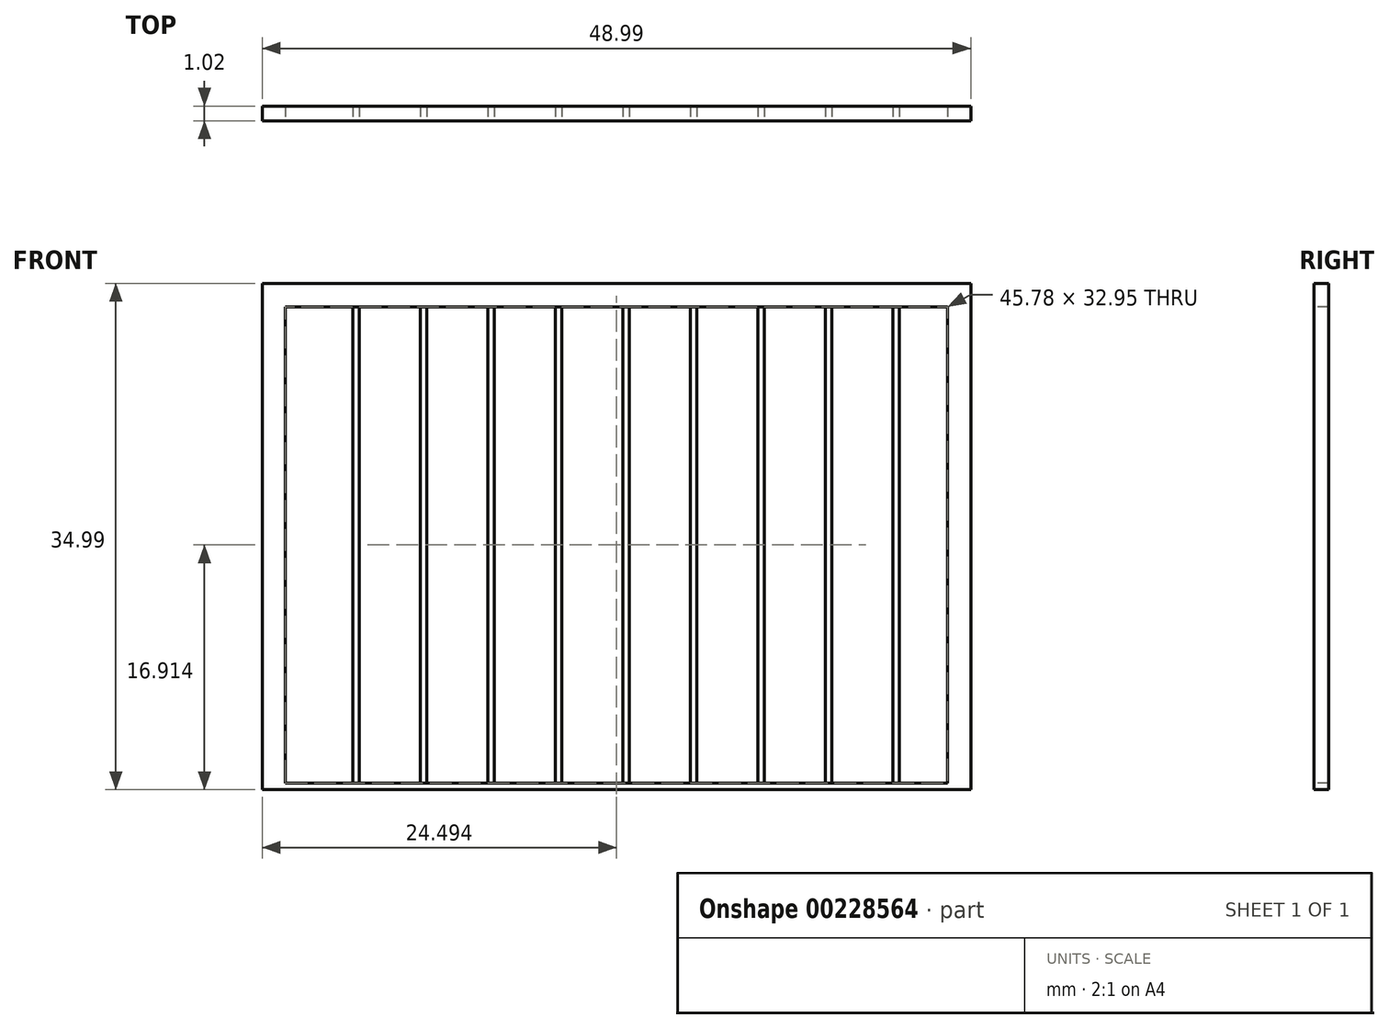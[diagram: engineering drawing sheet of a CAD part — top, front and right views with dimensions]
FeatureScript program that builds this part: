
annotation { "Feature Type Name" : "Feature", "Feature Type Description" : "" }
export const myFeature = defineFeature(function(context is Context, id is Id, definition is map)
    precondition{}
    {
        {
            var Q0;
            Q0=qCreatedBy(makeId("Front.planeOp"),FACE);
            var sketch = newSketch(context, id + "F0", { "sketchPlane" : qUnion([Q0])});
            skLineSegment(sketch, "E0.bottom", {"start": v(0, 0) * mm, "end": v(-4267.2, 0) * mm});
            skLineSegment(sketch, "E0.top", {"start": v(0, 3048) * mm, "end": v(-4267.2, 3048) * mm});
            skLineSegment(sketch, "E0.left", {"start": v(0, 0) * mm, "end": v(0, 3048) * mm});
            skLineSegment(sketch, "E0.right", {"start": v(-4267.2, 0) * mm, "end": v(-4267.2, 3048) * mm});
            skSolve(sketch);
        }
        {
            var Q0;
            Q0=makeQuery(id+"F0.imprint","IMPRINT",FACE,{"disambiguationData":[TD([[makeQuery(id+"F0.imprint","IMPRINT",EDGE,{"derivedFrom":sQuery(id+"F0.wireOp",EDGE,"E0.bottom")}),-1.0]])]});
            extrude(context, id + "F1", {"entities" : qUnion([Q0]), "depth" : 88.9 * mm});
        }
        {
            var Q0;
            Q0=makeQuery(id+"F1.opExtrude","CAP_FACE",FACE,{"disambiguationData":[OSD([sQuery(id+"F0.wireOp",EDGE,"E0.bottom"),sQuery(id+"F0.wireOp",EDGE,"E0.top"),sQuery(id+"F0.wireOp",EDGE,"E0.left"),sQuery(id+"F0.wireOp",EDGE,"E0.right")])],"isStart":true});
            var sketch = newSketch(context, id + "F2", { "sketchPlane" : qUnion([Q0])});
            skLineSegment(sketch, "E1", {"start": v(139.7, 0) * mm, "end": v(139.7, 2908.3) * mm});
            skLineSegment(sketch, "E2", {"start": v(139.7, 2908.3) * mm, "end": v(4127.5, 2908.3) * mm});
            skLineSegment(sketch, "E3", {"start": v(4127.5, 2908.3) * mm, "end": v(4127.5, 0) * mm});
            skLineSegment(sketch, "E4", {"start": v(4127.5, 0) * mm, "end": v(139.7, 0) * mm});
            skSolve(sketch);
        }
        {
            var Q0;
            Q0=makeQuery(id+"F2.imprint","IMPRINT",FACE,{"disambiguationData":[TD([[makeQuery(id+"F2.imprint","IMPRINT",EDGE,{"derivedFrom":sQuery(id+"F2.wireOp",EDGE,"E1")}),-1.0]])]});
            extrude(context, id + "F3", {"entities" : qUnion([Q0]), "operationType" : NewBodyOperationType.REMOVE, "endBound" : BoundingType.THROUGH_ALL, "oppositeDirection" : true, "depth" : 25.4 * mm});
        }
        {
            var Q0;
            Q0=makeQuery(id+"F1.opExtrude","CAP_FACE",FACE,{"disambiguationData":[OSD([sQuery(id+"F0.wireOp",EDGE,"E0.bottom"),sQuery(id+"F0.wireOp",EDGE,"E0.top"),sQuery(id+"F0.wireOp",EDGE,"E0.left"),sQuery(id+"F0.wireOp",EDGE,"E0.right")])],"isStart":false});
            var sketch = newSketch(context, id + "F4", { "sketchPlane" : qUnion([Q0])});
            skLineSegment(sketch, "E5.bottom", {"start": v(-4127.5, 0) * mm, "end": v(-139.7, 0) * mm});
            skLineSegment(sketch, "E5.top", {"start": v(-4127.5, 38.1) * mm, "end": v(-139.7, 38.1) * mm});
            skLineSegment(sketch, "E5.left", {"start": v(-4127.5, 0) * mm, "end": v(-4127.5, 38.1) * mm});
            skLineSegment(sketch, "E5.right", {"start": v(-139.7, 0) * mm, "end": v(-139.7, 38.1) * mm});
            skSolve(sketch);
        }
        {
            var Q0;
            Q0=makeQuery(id+"F4.imprint","IMPRINT",FACE,{"disambiguationData":[TD([[makeQuery(id+"F4.imprint","IMPRINT",EDGE,{"derivedFrom":sQuery(id+"F4.wireOp",EDGE,"E5.bottom")}),1.0]])]});
            extrude(context, id + "F5", {"entities" : qUnion([Q0]), "operationType" : NewBodyOperationType.ADD, "oppositeDirection" : true, "depth" : 88.9 * mm});
        }
        {
            var Q0;
            Q0=makeQuery(id+"F5.boolean.opBoolean","MERGE",FACE,{"derivedFrom":[makeQuery(id+"F1.opExtrude","CAP_FACE",FACE,{"disambiguationData":[OSD([sQuery(id+"F0.wireOp",EDGE,"E0.bottom"),sQuery(id+"F0.wireOp",EDGE,"E0.top"),sQuery(id+"F0.wireOp",EDGE,"E0.left"),sQuery(id+"F0.wireOp",EDGE,"E0.right")])],"isStart":false}),makeQuery(id+"F5.opExtrude","CAP_FACE",FACE,{"disambiguationData":[OSD([sQuery(id+"F4.wireOp",EDGE,"E5.bottom"),sQuery(id+"F4.wireOp",EDGE,"E5.top"),sQuery(id+"F4.wireOp",EDGE,"E5.left"),sQuery(id+"F4.wireOp",EDGE,"E5.right")])],"isStart":true})]});
            var sketch = newSketch(context, id + "F6", { "sketchPlane" : qUnion([Q0])});
            skLineSegment(sketch, "E6.bottom", {"start": v(-3721.1, 38.1) * mm, "end": v(-3683, 38.1) * mm});
            skLineSegment(sketch, "E6.top", {"start": v(-3721.1, 2908.3) * mm, "end": v(-3683, 2908.3) * mm});
            skLineSegment(sketch, "E6.left", {"start": v(-3721.1, 38.1) * mm, "end": v(-3721.1, 2908.3) * mm});
            skLineSegment(sketch, "E6.right", {"start": v(-3683, 38.1) * mm, "end": v(-3683, 2908.3) * mm});
            skLineSegment(sketch, "E7.1.0.0", {"start": v(-3314.7, 38.1) * mm, "end": v(-3314.7, 2908.3) * mm});
            skLineSegment(sketch, "E7.1.0.1", {"start": v(-3276.6, 38.1) * mm, "end": v(-3276.6, 2908.3) * mm});
            skLineSegment(sketch, "E7.1.0.2", {"start": v(-3314.7, 38.1) * mm, "end": v(-3276.6, 38.1) * mm});
            skLineSegment(sketch, "E7.1.0.3", {"start": v(-3314.7, 2908.3) * mm, "end": v(-3276.6, 2908.3) * mm});
            skLineSegment(sketch, "E7.2.0.0", {"start": v(-2908.3, 38.1) * mm, "end": v(-2908.3, 2908.3) * mm});
            skLineSegment(sketch, "E7.2.0.1", {"start": v(-2870.2, 38.1) * mm, "end": v(-2870.2, 2908.3) * mm});
            skLineSegment(sketch, "E7.2.0.2", {"start": v(-2908.3, 38.1) * mm, "end": v(-2870.2, 38.1) * mm});
            skLineSegment(sketch, "E7.2.0.3", {"start": v(-2908.3, 2908.3) * mm, "end": v(-2870.2, 2908.3) * mm});
            skLineSegment(sketch, "E7.3.0.0", {"start": v(-2501.9, 38.1) * mm, "end": v(-2501.9, 2908.3) * mm});
            skLineSegment(sketch, "E7.3.0.1", {"start": v(-2463.8, 38.1) * mm, "end": v(-2463.8, 2908.3) * mm});
            skLineSegment(sketch, "E7.3.0.2", {"start": v(-2501.9, 38.1) * mm, "end": v(-2463.8, 38.1) * mm});
            skLineSegment(sketch, "E7.3.0.3", {"start": v(-2501.9, 2908.3) * mm, "end": v(-2463.8, 2908.3) * mm});
            skLineSegment(sketch, "E7.4.0.0", {"start": v(-2095.5, 38.1) * mm, "end": v(-2095.5, 2908.3) * mm});
            skLineSegment(sketch, "E7.4.0.1", {"start": v(-2057.4, 38.1) * mm, "end": v(-2057.4, 2908.3) * mm});
            skLineSegment(sketch, "E7.4.0.2", {"start": v(-2095.5, 38.1) * mm, "end": v(-2057.4, 38.1) * mm});
            skLineSegment(sketch, "E7.4.0.3", {"start": v(-2095.5, 2908.3) * mm, "end": v(-2057.4, 2908.3) * mm});
            skLineSegment(sketch, "E7.5.0.0", {"start": v(-1689.1, 38.1) * mm, "end": v(-1689.1, 2908.3) * mm});
            skLineSegment(sketch, "E7.5.0.1", {"start": v(-1651, 38.1) * mm, "end": v(-1651, 2908.3) * mm});
            skLineSegment(sketch, "E7.5.0.2", {"start": v(-1689.1, 38.1) * mm, "end": v(-1651, 38.1) * mm});
            skLineSegment(sketch, "E7.5.0.3", {"start": v(-1689.1, 2908.3) * mm, "end": v(-1651, 2908.3) * mm});
            skLineSegment(sketch, "E7.6.0.0", {"start": v(-1282.7, 38.1) * mm, "end": v(-1282.7, 2908.3) * mm});
            skLineSegment(sketch, "E7.6.0.1", {"start": v(-1244.6, 38.1) * mm, "end": v(-1244.6, 2908.3) * mm});
            skLineSegment(sketch, "E7.6.0.2", {"start": v(-1282.7, 38.1) * mm, "end": v(-1244.6, 38.1) * mm});
            skLineSegment(sketch, "E7.6.0.3", {"start": v(-1282.7, 2908.3) * mm, "end": v(-1244.6, 2908.3) * mm});
            skLineSegment(sketch, "E7.7.0.0", {"start": v(-876.3, 38.1) * mm, "end": v(-876.3, 2908.3) * mm});
            skLineSegment(sketch, "E7.7.0.1", {"start": v(-838.2, 38.1) * mm, "end": v(-838.2, 2908.3) * mm});
            skLineSegment(sketch, "E7.7.0.2", {"start": v(-876.3, 38.1) * mm, "end": v(-838.2, 38.1) * mm});
            skLineSegment(sketch, "E7.7.0.3", {"start": v(-876.3, 2908.3) * mm, "end": v(-838.2, 2908.3) * mm});
            skLineSegment(sketch, "E7.8.0.0", {"start": v(-469.9, 38.1) * mm, "end": v(-469.9, 2908.3) * mm});
            skLineSegment(sketch, "E7.8.0.1", {"start": v(-431.8, 38.1) * mm, "end": v(-431.8, 2908.3) * mm});
            skLineSegment(sketch, "E7.8.0.2", {"start": v(-469.9, 38.1) * mm, "end": v(-431.8, 38.1) * mm});
            skLineSegment(sketch, "E7.8.0.3", {"start": v(-469.9, 2908.3) * mm, "end": v(-431.8, 2908.3) * mm});
            skLineSegment(sketch, "E7.direction1", {"start": v(-3721.1, 38.1) * mm, "end": v(-3314.7, 38.1) * mm, "construction": true});
            skSolve(sketch);
        }
        {
            var Q0;
            Q0=makeQuery(id+"F6.imprint","IMPRINT",FACE,{"disambiguationData":[TD([[makeQuery(id+"F6.imprint","IMPRINT",EDGE,{"derivedFrom":sQuery(id+"F6.wireOp",EDGE,"E6.bottom")}),1.0]])]});
            var Q1;
            Q1=makeQuery(id+"F6.imprint","IMPRINT",FACE,{"disambiguationData":[TD([[makeQuery(id+"F6.imprint","IMPRINT",EDGE,{"derivedFrom":sQuery(id+"F6.wireOp",EDGE,"E7.1.0.0")}),-1.0]])]});
            var Q2;
            Q2=makeQuery(id+"F6.imprint","IMPRINT",FACE,{"disambiguationData":[TD([[makeQuery(id+"F6.imprint","IMPRINT",EDGE,{"derivedFrom":sQuery(id+"F6.wireOp",EDGE,"E7.2.0.0")}),-1.0]])]});
            var Q3;
            Q3=makeQuery(id+"F6.imprint","IMPRINT",FACE,{"disambiguationData":[TD([[makeQuery(id+"F6.imprint","IMPRINT",EDGE,{"derivedFrom":sQuery(id+"F6.wireOp",EDGE,"E7.3.0.0")}),-1.0]])]});
            var Q4;
            Q4=makeQuery(id+"F6.imprint","IMPRINT",FACE,{"disambiguationData":[TD([[makeQuery(id+"F6.imprint","IMPRINT",EDGE,{"derivedFrom":sQuery(id+"F6.wireOp",EDGE,"E7.4.0.0")}),-1.0]])]});
            var Q5;
            Q5=makeQuery(id+"F6.imprint","IMPRINT",FACE,{"disambiguationData":[TD([[makeQuery(id+"F6.imprint","IMPRINT",EDGE,{"derivedFrom":sQuery(id+"F6.wireOp",EDGE,"E7.5.0.0")}),-1.0]])]});
            var Q6;
            Q6=makeQuery(id+"F6.imprint","IMPRINT",FACE,{"disambiguationData":[TD([[makeQuery(id+"F6.imprint","IMPRINT",EDGE,{"derivedFrom":sQuery(id+"F6.wireOp",EDGE,"E7.6.0.0")}),-1.0]])]});
            var Q7;
            Q7=makeQuery(id+"F6.imprint","IMPRINT",FACE,{"disambiguationData":[TD([[makeQuery(id+"F6.imprint","IMPRINT",EDGE,{"derivedFrom":sQuery(id+"F6.wireOp",EDGE,"E7.7.0.0")}),-1.0]])]});
            var Q8;
            Q8=makeQuery(id+"F6.imprint","IMPRINT",FACE,{"disambiguationData":[TD([[makeQuery(id+"F6.imprint","IMPRINT",EDGE,{"derivedFrom":sQuery(id+"F6.wireOp",EDGE,"E7.8.0.0")}),-1.0]])]});
            extrude(context, id + "F7", {"entities" : qUnion([Q0, Q1, Q2, Q3, Q4, Q5, Q6, Q7, Q8]), "oppositeDirection" : true, "depth" : 88.9 * mm});
        }
        {
            var Q0;
            Q0=makeQuery(id+"F7.opExtrude","SWEPT_BODY",BODY,{"disambiguationData":[OSD([sQuery(id+"F6.wireOp",EDGE,"E7.6.0.0"),sQuery(id+"F6.wireOp",EDGE,"E7.6.0.1"),sQuery(id+"F6.wireOp",EDGE,"E7.6.0.2"),sQuery(id+"F6.wireOp",EDGE,"E7.6.0.3")])]});
            var Q1;
            Q1=makeQuery(id+"F7.opExtrude","SWEPT_BODY",BODY,{"disambiguationData":[OSD([sQuery(id+"F6.wireOp",EDGE,"E7.8.0.0"),sQuery(id+"F6.wireOp",EDGE,"E7.8.0.1"),sQuery(id+"F6.wireOp",EDGE,"E7.8.0.2"),sQuery(id+"F6.wireOp",EDGE,"E7.8.0.3")])]});
            var Q2;
            Q2=makeQuery(id+"F7.opExtrude","SWEPT_BODY",BODY,{"disambiguationData":[OSD([sQuery(id+"F6.wireOp",EDGE,"E7.5.0.0"),sQuery(id+"F6.wireOp",EDGE,"E7.5.0.1"),sQuery(id+"F6.wireOp",EDGE,"E7.5.0.2"),sQuery(id+"F6.wireOp",EDGE,"E7.5.0.3")])]});
            var Q3;
            Q3=makeQuery(id+"F7.opExtrude","SWEPT_BODY",BODY,{"disambiguationData":[OSD([sQuery(id+"F6.wireOp",EDGE,"E7.3.0.0"),sQuery(id+"F6.wireOp",EDGE,"E7.3.0.1"),sQuery(id+"F6.wireOp",EDGE,"E7.3.0.2"),sQuery(id+"F6.wireOp",EDGE,"E7.3.0.3")])]});
            var Q4;
            Q4=makeQuery(id+"F7.opExtrude","SWEPT_BODY",BODY,{"disambiguationData":[OSD([sQuery(id+"F6.wireOp",EDGE,"E7.4.0.0"),sQuery(id+"F6.wireOp",EDGE,"E7.4.0.1"),sQuery(id+"F6.wireOp",EDGE,"E7.4.0.2"),sQuery(id+"F6.wireOp",EDGE,"E7.4.0.3")])]});
            var Q5;
            Q5=makeQuery(id+"F7.opExtrude","SWEPT_BODY",BODY,{"disambiguationData":[OSD([sQuery(id+"F6.wireOp",EDGE,"E7.2.0.0"),sQuery(id+"F6.wireOp",EDGE,"E7.2.0.1"),sQuery(id+"F6.wireOp",EDGE,"E7.2.0.2"),sQuery(id+"F6.wireOp",EDGE,"E7.2.0.3")])]});
            var Q6;
            Q6=makeQuery(id+"F7.opExtrude","SWEPT_BODY",BODY,{"disambiguationData":[OSD([sQuery(id+"F6.wireOp",EDGE,"E6.bottom"),sQuery(id+"F6.wireOp",EDGE,"E6.top"),sQuery(id+"F6.wireOp",EDGE,"E6.left"),sQuery(id+"F6.wireOp",EDGE,"E6.right")])]});
            var Q7;
            Q7=makeQuery(id+"F1.opExtrude","SWEPT_BODY",BODY,{"disambiguationData":[OSD([sQuery(id+"F0.wireOp",EDGE,"E0.bottom"),sQuery(id+"F0.wireOp",EDGE,"E0.top"),sQuery(id+"F0.wireOp",EDGE,"E0.left"),sQuery(id+"F0.wireOp",EDGE,"E0.right")])]});
            var Q8;
            Q8=makeQuery(id+"F7.opExtrude","SWEPT_BODY",BODY,{"disambiguationData":[OSD([sQuery(id+"F6.wireOp",EDGE,"E7.7.0.0"),sQuery(id+"F6.wireOp",EDGE,"E7.7.0.1"),sQuery(id+"F6.wireOp",EDGE,"E7.7.0.2"),sQuery(id+"F6.wireOp",EDGE,"E7.7.0.3")])]});
            var Q9;
            Q9=makeQuery(id+"F7.opExtrude","SWEPT_BODY",BODY,{"disambiguationData":[OSD([sQuery(id+"F6.wireOp",EDGE,"E7.1.0.0"),sQuery(id+"F6.wireOp",EDGE,"E7.1.0.1"),sQuery(id+"F6.wireOp",EDGE,"E7.1.0.2"),sQuery(id+"F6.wireOp",EDGE,"E7.1.0.3")])]});
            var Q10;
            Q10=qCreatedBy(makeId("Origin.pointOp"),VERTEX);
            transform(context, id + "F8", {"entities" : qUnion([Q0, Q1, Q2, Q3, Q4, Q5, Q6, Q7, Q8, Q9]), "transformType" : TransformType.SCALE_UNIFORMLY, "scale" : 1 / 87.1, "scalePoint" : qUnion([Q10]), "makeCopy" : false});
        }
    });
